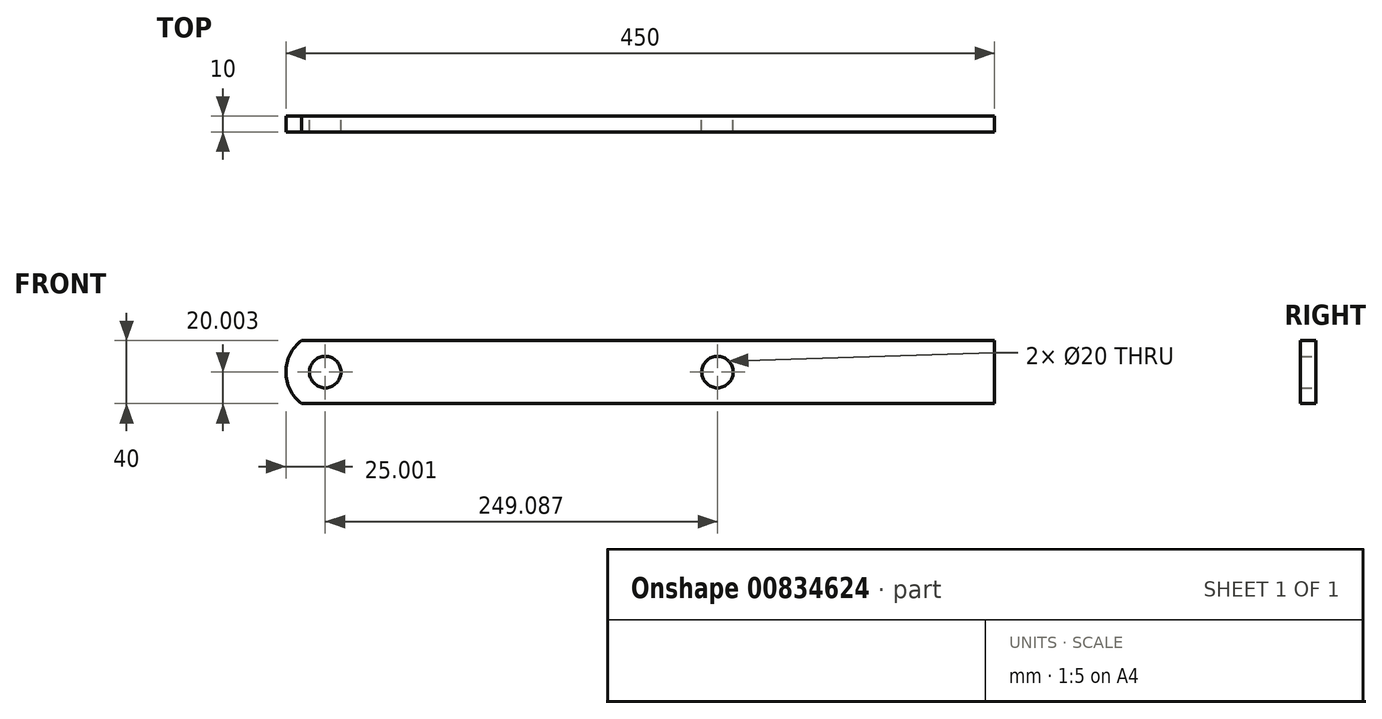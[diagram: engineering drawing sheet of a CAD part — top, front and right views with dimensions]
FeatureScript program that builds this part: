
annotation { "Feature Type Name" : "Feature", "Feature Type Description" : "" }
export const myFeature = defineFeature(function(context is Context, id is Id, definition is map)
    precondition{}
    {
        {
            var Q0;
            Q0=qCreatedBy(makeId("Front.planeOp"),FACE);
            var sketch = newSketch(context, id + "F0", { "sketchPlane" : qUnion([Q0])});
            skLineSegment(sketch, "E0", {"start": v(-219.03, -66.43) * mm, "end": v(220.97, -66.43) * mm});
            skLineSegment(sketch, "E1", {"start": v(220.97, -66.43) * mm, "end": v(220.97, -106.43) * mm});
            skLineSegment(sketch, "E2", {"start": v(220.97, -106.43) * mm, "end": v(-219.03, -106.43) * mm});
            skCircle(sketch, "E3", {"center": v(-204.03, -86.43) * mm, "radius": 10 * mm});
            skArc(sketch, "E4", {"start": v(-219.03, -66.43) * mm, "mid": v(-229.03, -86.43) * mm, "end": v(-219.03, -106.43) * mm});
            skCircle(sketch, "E5.MirrorC", {"center": v(45.06, -86.43) * mm, "radius": 10 * mm});
            skSolve(sketch);
        }
        {
            var Q0;
            Q0 = qSketchRegion(id + "F0", true);
            extrude(context, id + "F1", {"entities" : qUnion([Q0]), "depth" : 10 * mm, "offsetDistance" : 25 * mm});
        }
    });
